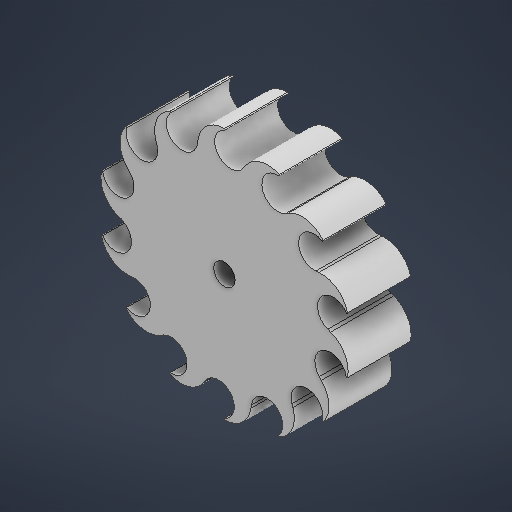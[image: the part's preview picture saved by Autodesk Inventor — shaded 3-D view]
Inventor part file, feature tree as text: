
AUTODESK INVENTOR PART (.ipt)
format: ipt  version: 2025.3 (Build 293356030, 356C)  size: 332,288 bytes
history: native  units: mm
features: sketch x2, extrude x1
ambient origin geometry x8: Origin, YZ Plane, XZ Plane, XY Plane, X Axis, Y Axis, Z Axis, Center Point
bodies: Solid1 (feature_tree)
feature tree (3):
  extrude  "Extrusion1"  Depth=60.0mm
  sketch  "Sketch1"  dims[d6=80.0mm d14=60.0mm]
  sketch  "Sketch Circular Pattern5"  dims[d16=0.2mm d22=5.0mm d23=60.0deg d28=6.0mm d29=140.0mm d31=360.0deg d33=6.8mm d34=20.0mm d35=0.0mm]
